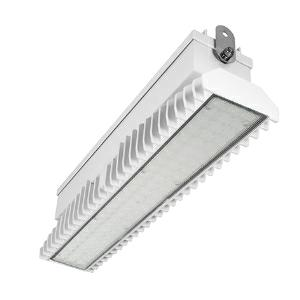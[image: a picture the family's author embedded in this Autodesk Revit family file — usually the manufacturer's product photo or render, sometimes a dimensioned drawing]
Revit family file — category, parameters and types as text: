
# Revit family: 3f_filippi_-_3f_lem_ho_concentrato_3f_filippi_-_58977_a0812_-_3f_lem_1_ho_led_70_dali_cr_conc___vs_ae5d
name_source: partatom
category: Lighting Fixtures
units: mm (PartAtom-declared; Revit-internal decimal feet)

## family parameters
Cut with Voids When Loaded = No
Host = Face
Light Source = No
Part Type = Normal
Room Calculation Point = No
Round Connector Dimension = Use Diameter
Shared = No

## types (1)
- 3F Filippi - 3F LEM HO Concentrato (1 x LED, 8791 lm, 71 W, 4000 K)
    Apparent Load = 71 VA
    Approval mark = CE
    CIE Flux Codes = 78 93 98 100 100
    Color Rendering = 80
    Color Temperature = 4000 K
    Control Gear = Electronic transformer
    Default Elevation = 1800 mm
    Description = Industrial luminaire with high light output and high luminous efficiency designed with the most innovative technologies for environments with temperature up to 55°C.

ILLUMINOTECHNICAL
Luminous efficiency 100% (DLOR 98%, ULOR 2%).
Initial luminous flux of the luminaire 8791 lm.
Direct symmetric narrow distribution: the illuminated area has a elliptical shape.
Installation Interdistance Transv.D = 0.60 x hu - Long.D = 0.91 x hu.
Tabular UGR (CIE 117 - 4H-8H; S=0.25H; 70/50/20): RUG 24.3 - 25.5.
Beam angle: 38° - 61°.
Luminous efficacy 124 lm/W.
Lifetime (L93/B10): 30000 h. (tq+25°C)
Lifetime (L90/B10): 50000 h. (tq+25°C)
Lifetime (L85/B10): 80000 h. (tq+25°C)
Lifetime (L80/B10): 100000 h. (tq+25°C)
Lifetime (L85/B10): 50000 h. (tq+55°C)
Sudden decreased luminous flux after 50000 hours: 0% (C0).
Photobiological safety in compliance with IEC/TR 62778: RG0 risk exempt, (IEC 62471).
In compliance with IEC/EN 62722-2-1 - IEC/EN 62717 standards.

SOURCE
Mid-Power linear LED module 70W/840.
Energy efficiency class (UE 2019/2020 - UE 2019/2015): C.
CIE 13.3 Colour rendering index: CRI >80 (R9 <50%).
IES TM-30 Fidelity Index: Rf = 84 Rg = 95.
CCT nominal colour temperature 4000 K.
Colour initial tolerance (MacAdam): SDCM 3.

MECHANICAL
Passive modular heatsinks in die-casted aluminium, painted in white colour.
To optimize the thermal management of the LED module, the heatsinks are oversized and provided with self-cleaning of cooling fins.
Wiring body in aluminium and galvanised steel anchored solidly to the sinks and thermally separated.
3F Lens lenses with high luminous efficiency, transparent methacrylate (PMMA), fixed to the LED modules.
Fixing brackets in stainless steel.
Luminaire with limited surface temperature. - D - (EN 60598-2-24)
Dimensions: 542x115 mm, height 154 mm. Weight 6.705 kg.
IP65 protection degree.
Mechanical strength to impacts IK06 (1 joule).
Glow-wire test resistance 650°C.

ELECTRICAL
Halogen Free DALI-2 DATI (Parts 251, 252, 253), PUSH-DIM, electronic wiring 230V-50/60Hz, power factor 0.97 at full load, THD <25%, constant output current, class I, 1 driver, 1 DALI addresse.
Power of the luminaire 71 W.
ENEC - CE.
SAFE FLICKER: PstLM=<1 and SVM=<0.4 (IEC TR 61547-1 and IEC TR 63158), to ensure a more comfortable and safe light.
Luminaire compliant with EN 60598-2-22 for power supply from a centralised emergency system CPSS (Central Power Supply System), not incorporated in the luminaire - high risk areas excluded. The default power and flux are 100% in AC and 15% in DC.
Ambient temperature from -30°C to +55°C.
Temperature class T6 max 85°C.
Quick connection via M25 5P connector with 9-13 mm tightening range.
Power unit positioned on a separate compartment by the LED module to ensure optimum temperatures of cabling components, to be inspectable and maintainable.
Relative humidity UR: <85%.

INSTALLATION
Ceiling / Suspended / Wall.
All accessories dedicated to this product are available on the Catalog and on our website www.3F-Filippi.com.

ACCESSORIES
A0812 - Anti-glare microprismatic VS moulded glass, tempered, not flammable, with sealing gasket.
One required for each light module. The pack contains 10 pieces.

APPLICATIONS
In commercial environments, exhibition and industrial areas, stores, open areas or with shelves.
Environments in which it is necessary a total protection against falling fragments (eg environments with foodstuffs or machines with moving parts or with extreme temperature changes), use luminaires with polycarbonate lenses.

LIGHT MANAGEMENT
Recommended minimum setting: 10%.
The luminaire, equipped with (DALI-2 DATI) driver, can be controlled manually with 3F Easy Dim technology or automatically/manually with wired or wireless DALI/D2D control systems.
The D2D driver guarantees interoperability with other devices with the same certification by making the following information available:
Device Data (Part 251), Energy Report (Part 252), Diagnosis & Maintenance (Part 253).
In electrical systems without a regulation system (manual or automatic) and DALI bus, a suitable jumper must be made on the DA-DA terminals of the appliance.

WARNING
Fixture not suitable for cold stores with an ambient temperature <0°C and/or relative humidity >85%.
Luminaire designed for disposal/recycling at end-of-life.
Replaceable (LED only) light source by a professional. Replaceable control gear by a professional.
    Height = 154 mm
    Lamp = 1 x LED
    Lamp Light Flux = 8791 lm
    Lamp Power = 71 W
    Lamp count = 1
    Length = 542 mm
    Lifetime = 50000 h
    Luminous efficacy = 124 lm/W
    Manufacturer = 3F Filippi
    ModVariant = No
    Model = 3F Filippi - 58977+A0812 - 3F LEM 1 HO LED 70 DALI CR CONC + VS
    Mounting Place = Ceiling
    Mounting Type = Pendant
    Number of Poles = 1
    OnlyDefault = Yes
    Power Factor = 1
    Product Name = 3F Filippi - 3F LEM HO Concentrato
    Product group = pendant luminaire
    ProductGroupID = 9
    Protection Class = Protection class I
    Protection Degree = IP 65
    RLX_Detail_Level = 1
    RLX_Emergency_Light_Flux = 0 lm
    RLX_Emergency_Type = 0
    RLX_Emergency_Type_DB = No
    RlxData = <blob elided: 92801 chars, md5=d9493e97>
    Socket = socket
    Standby Power = 0 W
    System Light Flux = 8791 lm
    System Power = 71 W
    Type Comments = Product without accessories
    Type Image = 3f_filippi_-_lem_1__a0812.jpg
    URL = http://relux.com
    VarID = ---
    Voltage = 0 V
    Weight = 0.00 kg
    Width = 115 mm

## geometry (parser evidence)
native form markers: Blend x4, Sweep x12
no freeform markers — native parametric forms only
